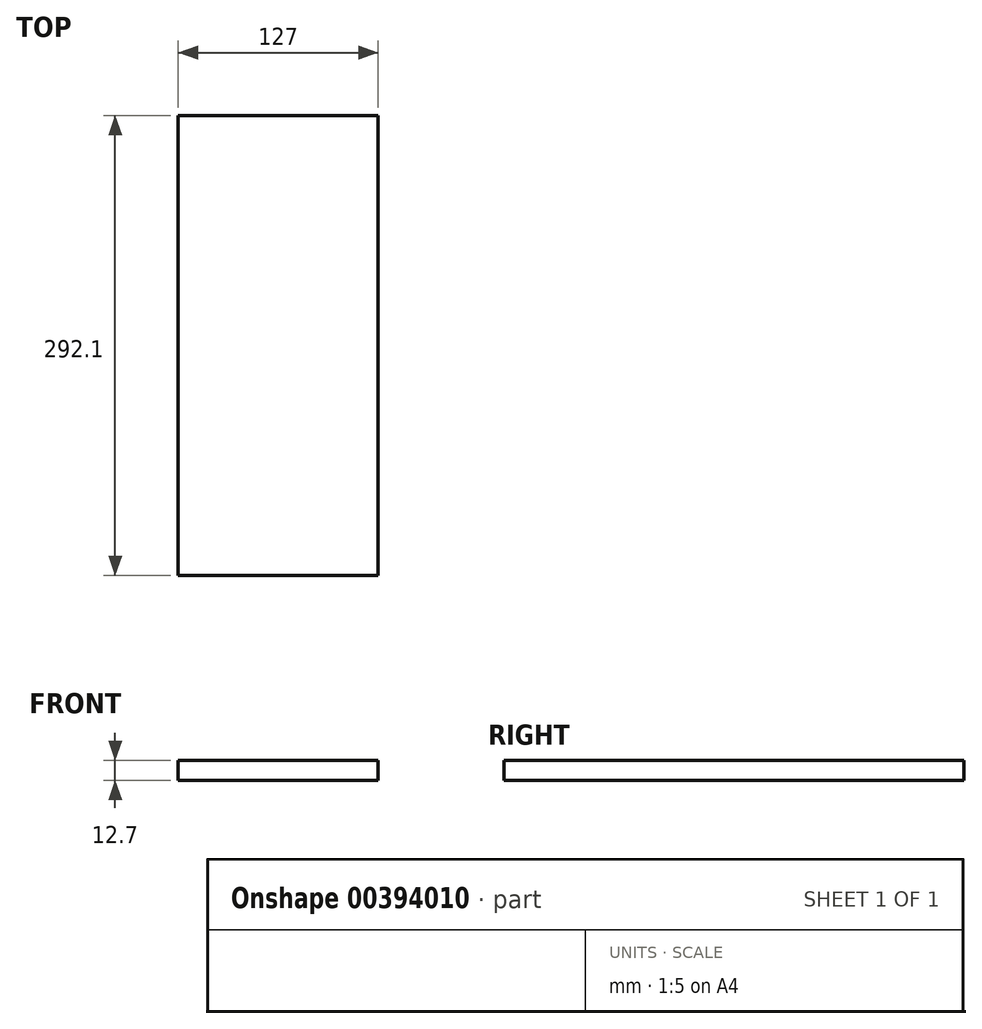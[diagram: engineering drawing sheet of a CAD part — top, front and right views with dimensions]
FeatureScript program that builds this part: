
annotation { "Feature Type Name" : "Feature", "Feature Type Description" : "" }
export const myFeature = defineFeature(function(context is Context, id is Id, definition is map)
    precondition{}
    {
        {
            var Q0;
            Q0=qCreatedBy(makeId("Top.planeOp"),FACE);
            var sketch = newSketch(context, id + "F0", { "sketchPlane" : qUnion([Q0])});
            skLineSegment(sketch, "E0.bottom", {"start": v(63.5, 146.05) * mm, "end": v(-63.5, 146.05) * mm});
            skLineSegment(sketch, "E0.top", {"start": v(63.5, -146.05) * mm, "end": v(-63.5, -146.05) * mm});
            skLineSegment(sketch, "E0.left", {"start": v(63.5, 146.05) * mm, "end": v(63.5, -146.05) * mm});
            skLineSegment(sketch, "E0.right", {"start": v(-63.5, 146.05) * mm, "end": v(-63.5, -146.05) * mm});
            skPoint(sketch, "E0.middle", {"position": v(0, 0) * mm});
            skSolve(sketch);
        }
        {
            var Q0;
            Q0=qSketchRegion(id+"F0",true);
            extrude(context, id + "F1", {"entities" : qUnion([Q0]), "depth" : 12.7 * mm});
        }
    });
